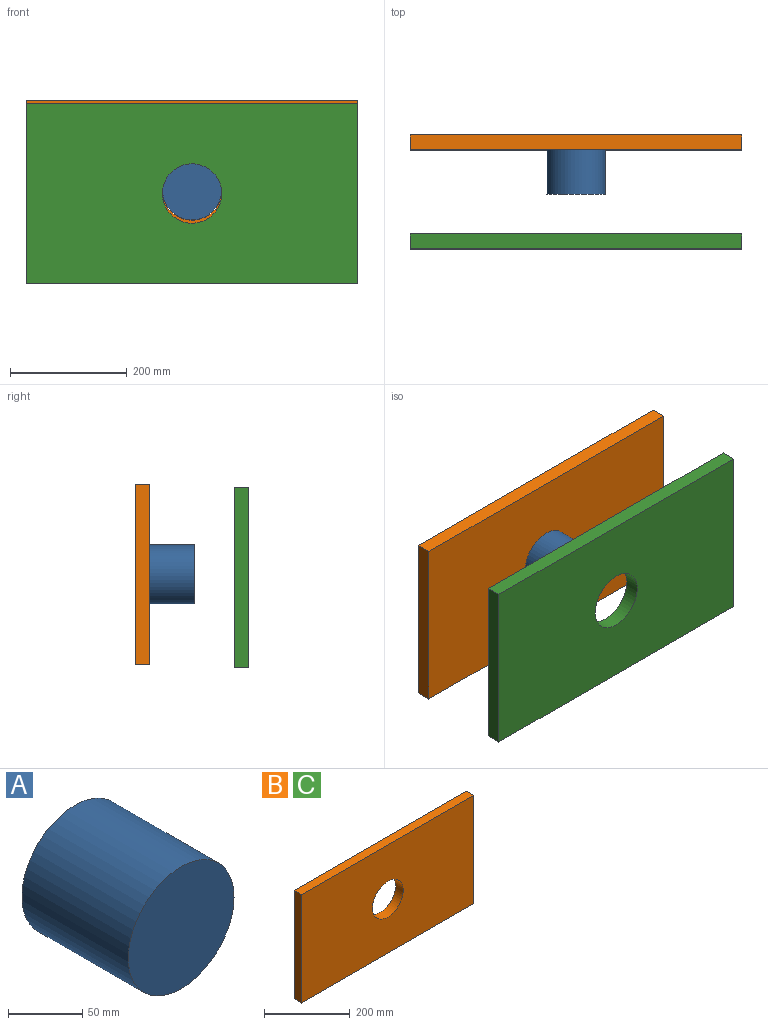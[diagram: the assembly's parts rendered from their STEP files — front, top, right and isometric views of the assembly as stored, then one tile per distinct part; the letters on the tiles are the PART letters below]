
ASSEMBLY  parts=3 mates=3
PART A: 3 faces, bbox 100.9x101.6x100.9 mm
  f0: cylinder r=50.46mm len=101.6mm, axis (0,1,0), area 32214.6mm2, adj f1,f2
  f1: plane 100.93x100.93mm, normal (0,-1,0), area 8000.4mm2, adj f0
  f2: plane 100.93x100.93mm, normal (0,1,0), area 8000.4mm2, adj f0
PART B: 7 faces, bbox 568.5x25.4x309.2 mm
  f0: plane 309.24x25.4mm, normal (-1,0,0), area 7854.7mm2, adj f1,f3,f5,f6
  f1: plane 568.54x25.4mm, normal (0,0,-1), area 14440.8mm2, adj f0,f2,f5,f6
  f2: plane 309.24x25.4mm, normal (1,0,0), area 7854.7mm2, adj f1,f3,f5,f6
  f3: plane 568.54x25.4mm, normal (0,0,1), area 14440.8mm2, adj f0,f2,f5,f6
  f4: cylinder r=50.86mm len=101.72mm, axis (0,1,0), area 8116.8mm2, adj f5,f6
  f5: plane 568.54x309.24mm, normal (0,-1,0), area 167688.1mm2, adj f0,f1,f2,f3,f4
  f6: plane 568.54x309.24mm, normal (0,1,0), area 167688.1mm2, adj f0,f1,f2,f3,f4
PART C: same geometry as B
PLACE A t=(-174.48,29.62,226.59)mm
PLACE B t=(-106.46,29.62,150.1)mm
PLACE C t=(-106.46,-139.92,144.77)mm
MATE parallel C.f4 <-> A.f0  axis (0,1,0) through (-174.48,-165.32,221.26)mm
MATE pin_slot B.f4 <-> A.f0  axis (0,1,0) through (-174.48,29.62,226.59)mm
MATE parallel C.f4 <-> A.f0  axis (0,1,0) through (-174.48,-139.92,221.26)mm
